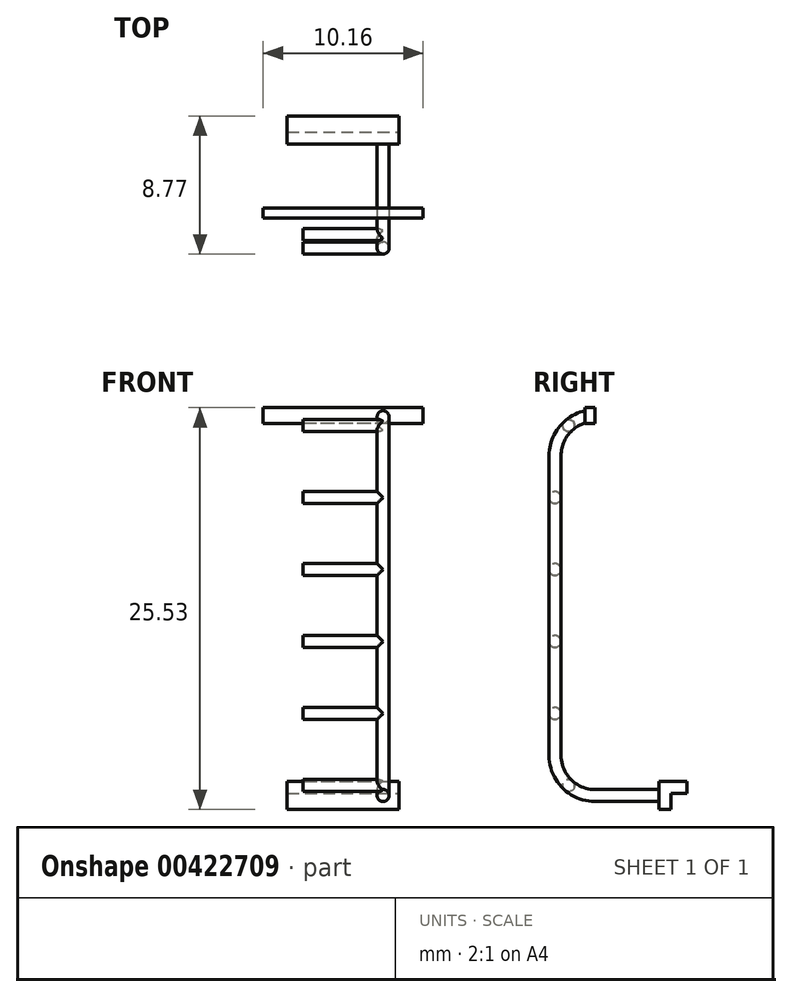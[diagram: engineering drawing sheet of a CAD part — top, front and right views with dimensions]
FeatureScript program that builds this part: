
annotation { "Feature Type Name" : "Feature", "Feature Type Description" : "" }
export const myFeature = defineFeature(function(context is Context, id is Id, definition is map)
    precondition{}
    {
        {
            var Q0;
            Q0=qCreatedBy(makeId("Front.planeOp"),FACE);
            var sketch = newSketch(context, id + "F0", { "sketchPlane" : qUnion([Q0])});
            skLineSegment(sketch, "E0.bottom", {"start": v(-3.56, 0) * mm, "end": v(3.56, 0) * mm});
            skLineSegment(sketch, "E0.top", {"start": v(-3.56, 1.78) * mm, "end": v(3.56, 1.78) * mm});
            skLineSegment(sketch, "E0.left", {"start": v(-3.56, 0) * mm, "end": v(-3.56, 1.78) * mm});
            skLineSegment(sketch, "E0.right", {"start": v(3.56, 0) * mm, "end": v(3.56, 1.78) * mm});
            skSolve(sketch);
        }
        {
            var Q0;
            Q0 = qSketchRegion(id + "F0", true);
            extrude(context, id + "F1", {"entities" : qUnion([Q0]), "depth" : 0.76 * mm});
        }
        {
            var Q0;
            Q0=makeQuery(id+"F1.opExtrude","CAP_FACE",FACE,{"disambiguationData":[OSD([sQuery(id+"F0.wireOp",EDGE,"E0.bottom"),sQuery(id+"F0.wireOp",EDGE,"E0.top"),sQuery(id+"F0.wireOp",EDGE,"E0.left"),sQuery(id+"F0.wireOp",EDGE,"E0.right")])],"isStart":true});
            var sketch = newSketch(context, id + "F2", { "sketchPlane" : qUnion([Q0])});
            skLineSegment(sketch, "E1.bottom", {"start": v(3.56, 1.78) * mm, "end": v(-3.56, 1.78) * mm});
            skLineSegment(sketch, "E1.top", {"start": v(3.56, 1.02) * mm, "end": v(-3.56, 1.02) * mm});
            skLineSegment(sketch, "E1.left", {"start": v(3.56, 1.78) * mm, "end": v(3.56, 1.02) * mm});
            skLineSegment(sketch, "E1.right", {"start": v(-3.56, 1.78) * mm, "end": v(-3.56, 1.02) * mm});
            skSolve(sketch);
        }
        {
            var Q0;
            Q0 = qSketchRegion(id + "F2", true);
            extrude(context, id + "F3", {"entities" : qUnion([Q0]), "operationType" : NewBodyOperationType.ADD, "depth" : 1.02 * mm});
        }
        {
            var Q0;
            Q0=qCreatedBy(makeId("Right.planeOp"),FACE);
            cPlane(context, id + "F4", {"entities" : qUnion([Q0]), "cplaneType" : CPlaneType.OFFSET, "offset" : 2.54 * mm, "width" : 152.4 * mm, "height" : 152.4 * mm});
        }
        {
            var Q0;
            Q0=qCreatedBy(id+"F4.planeOp",FACE);
            var sketch = newSketch(context, id + "F5", { "sketchPlane" : qUnion([Q0])});
            skLineSegment(sketch, "E2", {"start": v(-0.76, 0.89) * mm, "end": v(-4.83, 0.89) * mm});
            skLineSegment(sketch, "E3", {"start": v(-7.37, 3.43) * mm, "end": v(-7.37, 22.48) * mm});
            skLineSegment(sketch, "E4", {"start": v(-4.83, 25.02) * mm, "end": v(-4.83, 25.02) * mm});
            skPoint(sketch, "E5.visualSharp", {"position": v(-7.37, 0.89) * mm});
            skArc(sketch, "E5.filletArc", {"start": v(-7.37, 3.43) * mm, "mid": v(-6.62, 1.63) * mm, "end": v(-4.83, 0.89) * mm});
            skPoint(sketch, "E6.visualSharp", {"position": v(-7.37, 25.02) * mm});
            skArc(sketch, "E6.filletArc", {"start": v(-4.83, 25.02) * mm, "mid": v(-6.62, 24.28) * mm, "end": v(-7.37, 22.48) * mm});
            skSolve(sketch);
        }
        {
            var Q0;
            Q0=makeQuery(id+"F1.opExtrude","CAP_FACE",FACE,{"disambiguationData":[OSD([sQuery(id+"F0.wireOp",EDGE,"E0.bottom"),sQuery(id+"F0.wireOp",EDGE,"E0.top"),sQuery(id+"F0.wireOp",EDGE,"E0.left"),sQuery(id+"F0.wireOp",EDGE,"E0.right")])],"isStart":false});
            var sketch = newSketch(context, id + "F6", { "sketchPlane" : qUnion([Q0])});
            skCircle(sketch, "E7", {"center": v(2.54, 0.89) * mm, "radius": 0.38 * mm});
            skSolve(sketch);
        }
        {
            var Q0;
            Q0=makeQuery(id+"F6.imprint","IMPRINT",FACE,{"disambiguationData":[TD([[makeQuery(id+"F6.imprint","IMPRINT",EDGE,{"derivedFrom":sQuery(id+"F6.wireOp",EDGE,"E7")}),1.0]])]});
            var Q1;
            Q1 = qConstructionFilter(qBodyType(qCreatedBy(id + "F5" ,EDGE), BodyType.WIRE), ConstructionObject.NO);
            sweep(context, id + "F7", {"operationType" : NewBodyOperationType.ADD, "profiles" : qUnion([Q0]), "path" : qUnion([Q1])});
        }
        {
            var Q0;
            Q0=makeQuery(id+"F7.opSweep","CAP_FACE",FACE,{"disambiguationData":[OSD([sQuery(id+"F5.wireOp",VERTEX,"E4.end"),sQuery(id+"F6.wireOp",EDGE,"E7")])],"isStart":false});
            var sketch = newSketch(context, id + "F8", { "sketchPlane" : qUnion([Q0])});
            skLineSegment(sketch, "E8.bottom", {"start": v(-5.08, 25.53) * mm, "end": v(5.08, 25.53) * mm});
            skLineSegment(sketch, "E8.top", {"start": v(-5.08, 24.51) * mm, "end": v(5.08, 24.51) * mm});
            skLineSegment(sketch, "E8.left", {"start": v(-5.08, 25.53) * mm, "end": v(-5.08, 24.51) * mm});
            skLineSegment(sketch, "E8.right", {"start": v(5.08, 25.53) * mm, "end": v(5.08, 24.51) * mm});
            skSolve(sketch);
        }
        {
            var Q0;
            Q0 = qSketchRegion(id + "F8", true);
            extrude(context, id + "F9", {"entities" : qUnion([Q0]), "operationType" : NewBodyOperationType.ADD, "oppositeDirection" : true, "depth" : 0.64 * mm});
        }
        {
            var Q0;
            Q0=qCreatedBy(id+"F4.planeOp",FACE);
            var sketch = newSketch(context, id + "F10", { "sketchPlane" : qUnion([Q0])});
            skCircle(sketch, "E9", {"center": v(-6.5, 1.52) * mm, "radius": 0.38 * mm});
            skCircle(sketch, "E10", {"center": v(-7.37, 6.1) * mm, "radius": 0.38 * mm});
            skCircle(sketch, "E11", {"center": v(-7.37, 10.67) * mm, "radius": 0.38 * mm});
            skCircle(sketch, "E12", {"center": v(-7.37, 15.24) * mm, "radius": 0.38 * mm});
            skCircle(sketch, "E13", {"center": v(-7.37, 19.81) * mm, "radius": 0.38 * mm});
            skCircle(sketch, "E14", {"center": v(-6.5, 24.38) * mm, "radius": 0.38 * mm});
            skSolve(sketch);
        }
        {
            var Q0;
            Q0 = qSketchRegion(id + "F10", true);
            extrude(context, id + "F11", {"entities" : qUnion([Q0]), "operationType" : NewBodyOperationType.ADD, "oppositeDirection" : true, "depth" : 5.08 * mm});
        }
    });
